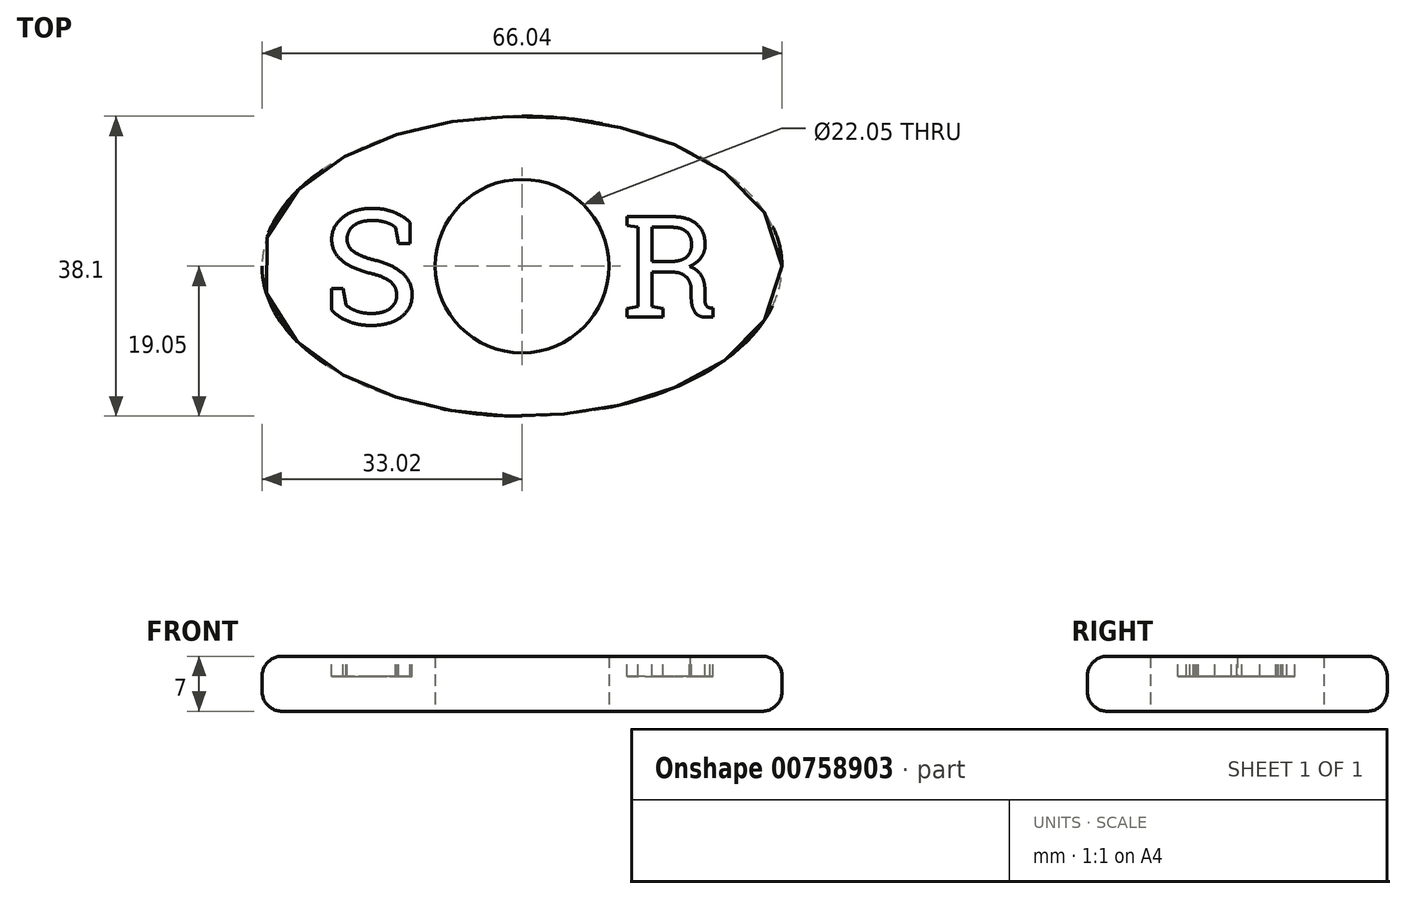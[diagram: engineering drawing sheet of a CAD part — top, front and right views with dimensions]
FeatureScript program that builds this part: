
annotation { "Feature Type Name" : "Feature", "Feature Type Description" : "" }
export const myFeature = defineFeature(function(context is Context, id is Id, definition is map)
    precondition{}
    {
        {
            var Q0;
            Q0=qCreatedBy(makeId("Top.planeOp"),FACE);
            var sketch = newSketch(context, id + "F0", { "sketchPlane" : qUnion([Q0])});
            skEllipse(sketch, "E0", {"center": v(0, 0) * mm, "majorRadius": 33.02 * mm, "minorRadius": 19.05 * mm, "majorAxis": v(1, 0)});
            skCircle(sketch, "E1", {"center": v(0, 0) * mm, "radius": 11.03 * mm});
            skLineSegment(sketch, "E2", {"start": v(-33.02, 0) * mm, "end": v(33.02, 0) * mm, "construction": true});
            skLineSegment(sketch, "E3", {"start": v(0, 19.05) * mm, "end": v(0, -19.05) * mm, "construction": true});
            skSolve(sketch);
        }
        {
            var Q0;
            Q0=makeQuery(id+"F0.imprint","IMPRINT",FACE,{"disambiguationData":[TD([[makeQuery(id+"F0.imprint","IMPRINT",EDGE,{"derivedFrom":sQuery(id+"F0.wireOp",EDGE,"E0")}),1.0]])]});
            extrude(context, id + "F1", {"entities" : qUnion([Q0]), "depth" : 7 * mm, "offsetDistance" : 25.4 * mm});
        }
        {
            var Q0;
            Q0=makeQuery(id+"F1.opExtrude","CAP_EDGE",EDGE,{"disambiguationData":[OSD([sQuery(id+"F0.wireOp",EDGE,"E0")])],"isStart":false});
            var Q1;
            Q1=makeQuery(id+"F1.opExtrude","CAP_EDGE",EDGE,{"disambiguationData":[OSD([sQuery(id+"F0.wireOp",EDGE,"E0")])],"isStart":true});
            fillet(context, id + "F2", {"entities" : qUnion([Q0, Q1]), "radius" : 2.54 * mm, "tangentPropagation" : true, "allowEdgeOverflow" : false});
        }
        {
            var Q0;
            Q0=makeQuery(id+"F1.opExtrude","CAP_FACE",FACE,{"disambiguationData":[OSD([sQuery(id+"F0.wireOp",EDGE,"E0"),sQuery(id+"F0.wireOp",EDGE,"E1")])],"isStart":false});
            var sketch = newSketch(context, id + "F3", { "sketchPlane" : qUnion([Q0])});
            skSolve(sketch);
        }
        {
            var Q0;
            {var subQ0=sQuery(id+"F0.wireOp",EDGE,"E1");Q0=makeQuery(id+"F3.imprint","IMPRINT",FACE,{"disambiguationData":[TD([[makeQuery(id+"F3.imprint","IMPRINT",EDGE,{"derivedFrom":makeQuery(id+"F1.opExtrude","CAP_EDGE",EDGE,{"disambiguationData":[OSD([subQ0])],"isStart":false})}),-1.0]])]});}
            var sketch = newSketch(context, id + "F4", { "sketchPlane" : qUnion([Q0])});
            skText(sketch, "E4", { "text": "S", "fontName": "RobotoSlab-Regular.ttf"});
            skText(sketch, "E5", { "text": "R", "fontName": "RobotoSlab-Regular.ttf"});
            skLineSegment(sketch, "E6", {"start": v(0, 0) * mm, "end": v(-25.4, 0) * mm, "construction": true});
            skLineSegment(sketch, "E7", {"start": v(0, 0) * mm, "end": v(25.4, 0) * mm, "construction": true});
            skLineSegment(sketch, "E8", {"start": v(-25.4, 0) * mm, "end": v(-12.7, 0) * mm, "construction": true});
            skLineSegment(sketch, "E9", {"start": v(12.7, 0) * mm, "end": v(25.4, 0) * mm});
            skPoint(sketch, "E10", {"position": v(19.05, 0) * mm});
            skLineSegment(sketch, "E11", {"start": v(12.7, 0) * mm, "end": v(25.4, 0) * mm, "construction": true});
            skPoint(sketch, "E12", {"position": v(-19.05, 0) * mm});
            const initialGuessF4  = {"E4": [-0.0254, -0.00733, 1, 0, 0.01465], "E5": [0.0127, -0.00648, 1, 0, 0.01295]};
            skSetInitialGuess(sketch, initialGuessF4);
            skSolve(sketch);
        }
        {
            var Q0;
            Q0=qSketchRegion(id+"F4",true);
            extrude(context, id + "F5", {"entities" : qUnion([Q0]), "operationType" : NewBodyOperationType.REMOVE, "oppositeDirection" : true, "depth" : 2.54 * mm, "offsetDistance" : 25.4 * mm});
        }
    });
